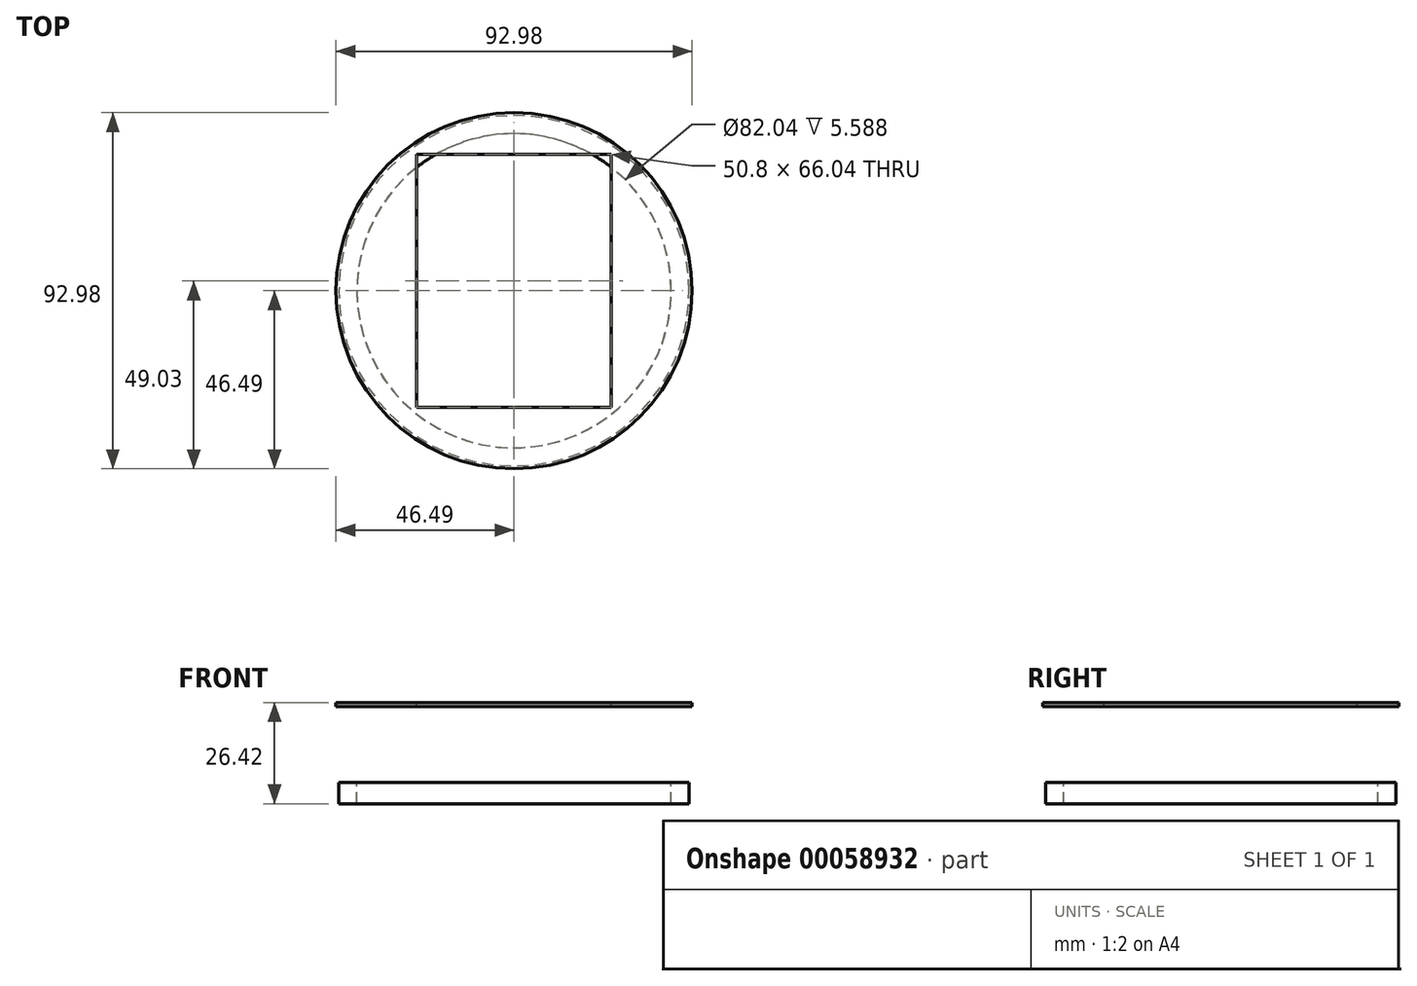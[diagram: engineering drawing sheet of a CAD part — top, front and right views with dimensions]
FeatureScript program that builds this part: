
annotation { "Feature Type Name" : "Feature", "Feature Type Description" : "" }
export const myFeature = defineFeature(function(context is Context, id is Id, definition is map)
    precondition{}
    {
        {
            var Q0;
            Q0=qCreatedBy(makeId("Top.planeOp"),FACE);
            var sketch = newSketch(context, id + "F0", { "sketchPlane" : qUnion([Q0])});
            skCircle(sketch, "E0", {"center": v(0, 0) * mm, "radius": 45.72 * mm});
            skSolve(sketch);
        }
        {
            var Q0;
            Q0 = qSketchRegion(id + "F0", true);
            extrude(context, id + "F1", {"entities" : qUnion([Q0]), "depth" : 5.6 * mm});
        }
        {
            var Q0;
            Q0=makeQuery(id+"F1.opExtrude","CAP_FACE",FACE,{"disambiguationData":[OSD([sQuery(id+"F0.wireOp",EDGE,"E0")])],"isStart":false});
            var sketch = newSketch(context, id + "F2", { "sketchPlane" : qUnion([Q0])});
            skCircle(sketch, "E1", {"center": v(0, 0) * mm, "radius": 41.02 * mm});
            skSolve(sketch);
        }
        {
            var Q0;
            Q0 = qSketchRegion(id + "F2", true);
            extrude(context, id + "F3", {"entities" : qUnion([Q0]), "operationType" : NewBodyOperationType.REMOVE, "endBound" : BoundingType.THROUGH_ALL, "oppositeDirection" : true, "depth" : 25.4 * mm});
        }
        {
            var Q0;
            Q0=qCreatedBy(makeId("Top.planeOp"),FACE);
            cPlane(context, id + "F4", {"entities" : qUnion([Q0]), "cplaneType" : CPlaneType.OFFSET, "offset" : 25.4 * mm, "width" : 152.4 * mm, "height" : 152.4 * mm});
        }
        {
            var Q0;
            Q0=qCreatedBy(id+"F4.planeOp",FACE);
            var sketch = newSketch(context, id + "F5", { "sketchPlane" : qUnion([Q0])});
            skCircle(sketch, "E2", {"center": v(0, 0) * mm, "radius": 46.49 * mm});
            skSolve(sketch);
        }
        {
            var Q0;
            Q0 = qSketchRegion(id + "F5", true);
            extrude(context, id + "F6", {"entities" : qUnion([Q0]), "depth" : 1.02 * mm});
        }
        {
            var Q0;
            Q0=makeQuery(id+"F6.opExtrude","CAP_FACE",FACE,{"disambiguationData":[OSD([sQuery(id+"F5.wireOp",EDGE,"E2")])],"isStart":false});
            var sketch = newSketch(context, id + "F7", { "sketchPlane" : qUnion([Q0])});
            skLineSegment(sketch, "E3.bottom", {"start": v(25.4, -30.48) * mm, "end": v(-25.4, -30.48) * mm});
            skLineSegment(sketch, "E3.top", {"start": v(25.4, 35.56) * mm, "end": v(-25.4, 35.56) * mm});
            skLineSegment(sketch, "E3.left", {"start": v(25.4, -30.48) * mm, "end": v(25.4, 35.56) * mm});
            skLineSegment(sketch, "E3.right", {"start": v(-25.4, -30.48) * mm, "end": v(-25.4, 35.56) * mm});
            skPoint(sketch, "E3.middle", {"position": v(0, 2.54) * mm});
            skSolve(sketch);
        }
        {
            var Q0;
            Q0 = qSketchRegion(id + "F7", true);
            extrude(context, id + "F8", {"entities" : qUnion([Q0]), "operationType" : NewBodyOperationType.REMOVE, "oppositeDirection" : true, "depth" : 12.7 * mm});
        }
    });
